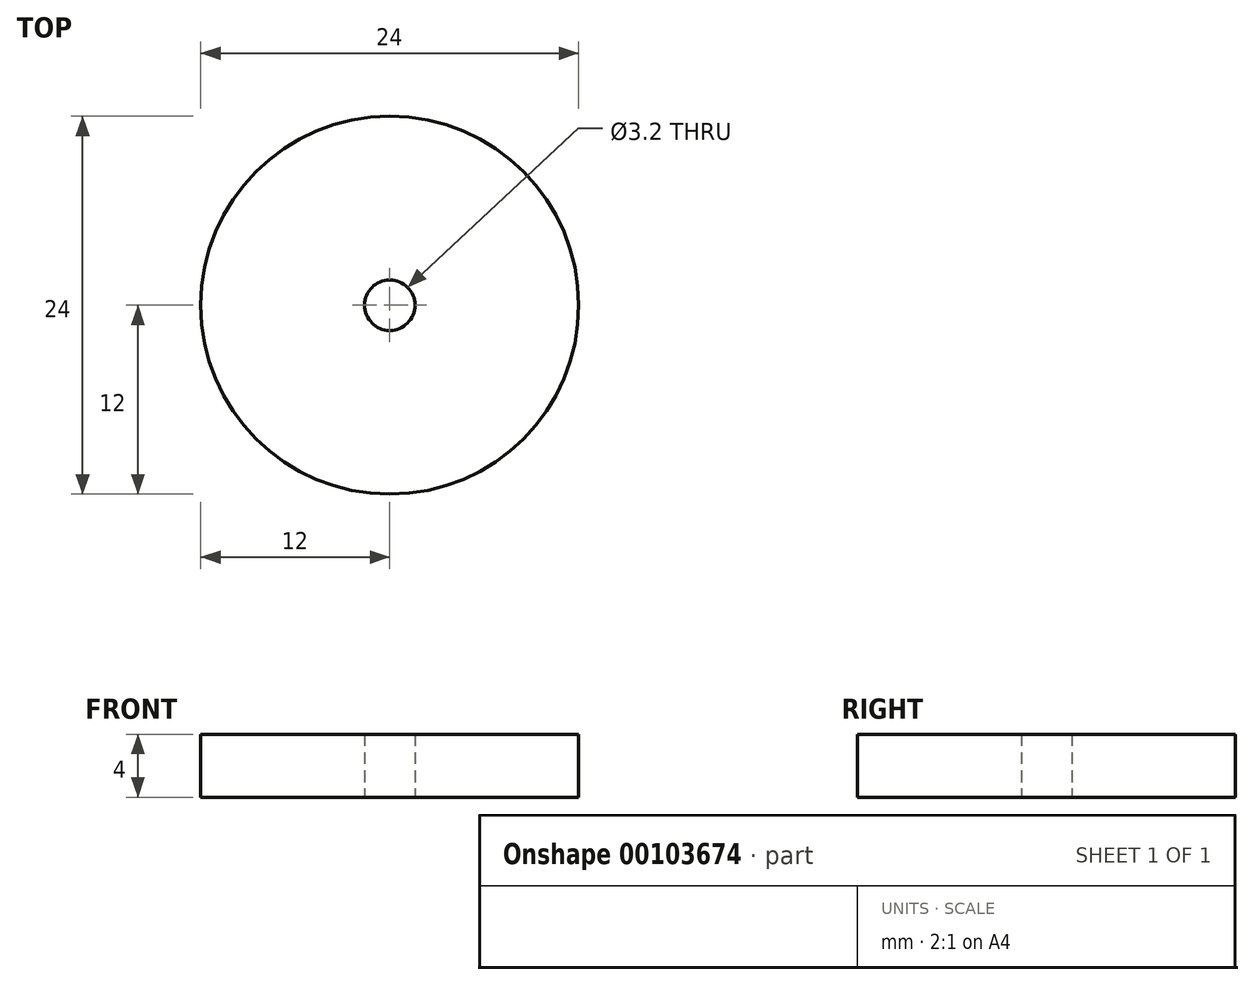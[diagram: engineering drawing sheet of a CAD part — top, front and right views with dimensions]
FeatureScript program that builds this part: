
annotation { "Feature Type Name" : "Feature", "Feature Type Description" : "" }
export const myFeature = defineFeature(function(context is Context, id is Id, definition is map)
    precondition{}
    {
        {
            var Q0;
            Q0=qCreatedBy(makeId("Top.planeOp"),FACE);
            var sketch = newSketch(context, id + "F0", { "sketchPlane" : qUnion([Q0])});
            skCircle(sketch, "E0", {"center": v(0, 0) * mm, "radius": 12 * mm});
            skCircle(sketch, "E1", {"center": v(0, 0) * mm, "radius": 1.6 * mm});
            skSolve(sketch);
        }
        {
            var Q0;
            Q0=makeQuery(id+"F0.imprint","IMPRINT",FACE,{"disambiguationData":[TD([[makeQuery(id+"F0.imprint","IMPRINT",EDGE,{"derivedFrom":sQuery(id+"F0.wireOp",EDGE,"E0")}),1.0]])]});
            extrude(context, id + "F1", {"entities" : qUnion([Q0]), "depth" : 4 * mm});
        }
    });
